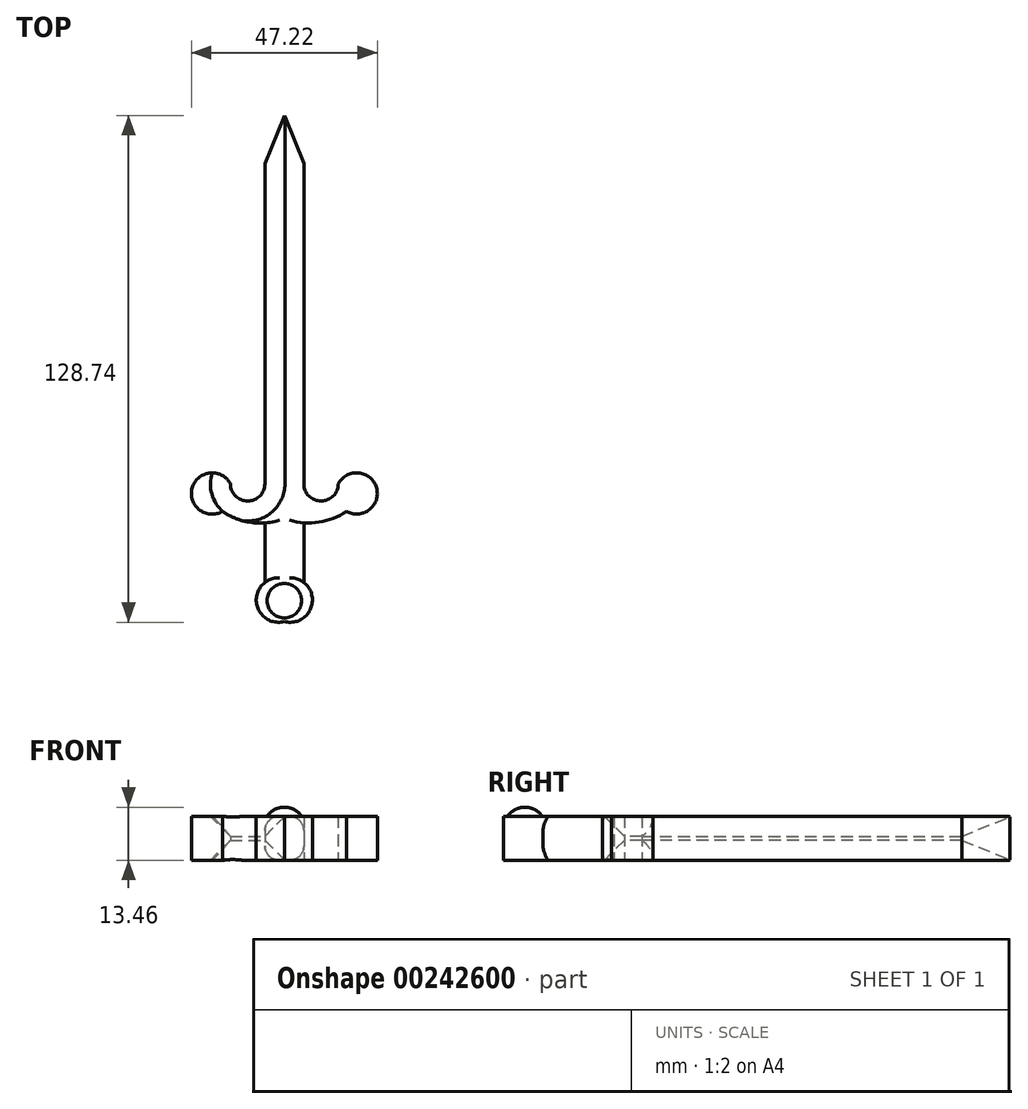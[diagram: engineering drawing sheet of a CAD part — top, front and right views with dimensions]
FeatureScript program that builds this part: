
annotation { "Feature Type Name" : "Feature", "Feature Type Description" : "" }
export const myFeature = defineFeature(function(context is Context, id is Id, definition is map)
    precondition{}
    {
        {
            var Q0;
            Q0=qCreatedBy(makeId("Top.planeOp"),FACE);
            var sketch = newSketch(context, id + "F0", { "sketchPlane" : qUnion([Q0])});
            skLineSegment(sketch, "E0", {"start": v(0, 64.85) * mm, "end": v(4.96, 52.61) * mm});
            skLineSegment(sketch, "E1", {"start": v(4.96, 52.61) * mm, "end": v(4.96, -28.71) * mm});
            skArc(sketch, "E2", {"start": v(4.96, -28.71) * mm, "mid": v(9.33, -33.08) * mm, "end": v(13.7, -28.71) * mm});
            skArc(sketch, "E3", {"start": v(15.74, -35.7) * mm, "mid": v(23.4, -29.68) * mm, "end": v(13.7, -28.71) * mm});
            skArc(sketch, "E4", {"start": v(4.96, -38.62) * mm, "mid": v(10.6, -38.07) * mm, "end": v(15.74, -35.7) * mm});
            skLineSegment(sketch, "E5", {"start": v(4.96, -38.62) * mm, "end": v(4.96, -53.78) * mm});
            skArc(sketch, "E6", {"start": v(0, -63.69) * mm, "mid": v(6.54, -60.76) * mm, "end": v(4.96, -53.78) * mm});
            skLineSegment(sketch, "E7.MirrorCS", {"start": v(0, 64.85) * mm, "end": v(-4.96, 52.61) * mm});
            skLineSegment(sketch, "E8.MirrorCS", {"start": v(-4.96, 52.61) * mm, "end": v(-4.96, -28.71) * mm});
            skArc(sketch, "E9.MirrorCS", {"start": v(-4.96, -28.71) * mm, "mid": v(-9.33, -33.08) * mm, "end": v(-13.7, -28.71) * mm});
            skArc(sketch, "E10.MirrorCS", {"start": v(-15.74, -35.7) * mm, "mid": v(-23.4, -29.68) * mm, "end": v(-13.7, -28.71) * mm});
            skArc(sketch, "E11.MirrorCS", {"start": v(-4.96, -38.62) * mm, "mid": v(-10.6, -38.07) * mm, "end": v(-15.74, -35.7) * mm});
            skLineSegment(sketch, "E12.MirrorCS", {"start": v(-4.96, -38.62) * mm, "end": v(-4.96, -53.78) * mm});
            skArc(sketch, "E13.MirrorCS", {"start": v(0, -63.69) * mm, "mid": v(-6.54, -60.76) * mm, "end": v(-4.96, -53.78) * mm});
            skSolve(sketch);
        }
        {
            var Q0;
            Q0=makeQuery(id+"F0.imprint","IMPRINT",FACE,{"disambiguationData":[TD([[makeQuery(id+"F0.imprint","IMPRINT",EDGE,{"derivedFrom":sQuery(id+"F0.wireOp",EDGE,"E0")}),-1.0]])]});
            extrude(context, id + "F1", {"entities" : qUnion([Q0]), "depth" : 11.18 * mm});
        }
        {
            var Q0;
            Q0=makeQuery(id+"F1.opExtrude","CAP_EDGE",EDGE,{"disambiguationData":[OSD([sQuery(id+"F0.wireOp",EDGE,"E8.MirrorCS")])],"isStart":false});
            var Q1;
            Q1=makeQuery(id+"F1.opExtrude","CAP_EDGE",EDGE,{"disambiguationData":[OSD([sQuery(id+"F0.wireOp",EDGE,"E1")])],"isStart":false});
            var Q2;
            Q2=makeQuery(id+"F1.opExtrude","CAP_EDGE",EDGE,{"disambiguationData":[OSD([sQuery(id+"F0.wireOp",EDGE,"E8.MirrorCS")])],"isStart":true});
            var Q3;
            Q3=makeQuery(id+"F1.opExtrude","CAP_EDGE",EDGE,{"disambiguationData":[OSD([sQuery(id+"F0.wireOp",EDGE,"E1")])],"isStart":true});
            chamfer(context, id + "F2", {"entities" : qUnion([Q0, Q1, Q2, Q3]), "width" : 5.08 * mm, "tangentPropagation" : true});
        }
        {
            var Q0;
            Q0=makeQuery(id+"F1.opExtrude","CAP_EDGE",EDGE,{"disambiguationData":[OSD([sQuery(id+"F0.wireOp",EDGE,"E12.MirrorCS")])],"isStart":false});
            fillet(context, id + "F3", {"entities" : qUnion([Q0]), "radius" : 3.68 * mm, "tangentPropagation" : true, "allowEdgeOverflow" : false});
        }
        {
            var Q0;
            Q0=makeQuery(id+"F1.opExtrude","CAP_EDGE",EDGE,{"disambiguationData":[OSD([sQuery(id+"F0.wireOp",EDGE,"E5")])],"isStart":false});
            var Q1;
            Q1=makeQuery(id+"F1.opExtrude","CAP_EDGE",EDGE,{"disambiguationData":[OSD([sQuery(id+"F0.wireOp",EDGE,"E5")])],"isStart":true});
            var Q2;
            Q2=makeQuery(id+"F1.opExtrude","CAP_EDGE",EDGE,{"disambiguationData":[OSD([sQuery(id+"F0.wireOp",EDGE,"E12.MirrorCS")])],"isStart":true});
            fillet(context, id + "F4", {"entities" : qUnion([Q0, Q1, Q2]), "radius" : 3.68 * mm, "tangentPropagation" : true, "allowEdgeOverflow" : false});
        }
        {
            var Q0;
            Q0=makeQuery(id+"F2.opChamfer","SPLIT",FACE,{"disambiguationData":[OD(2.0)],"derivedFrom":makeQuery(id+"F1.opExtrude","CAP_FACE",FACE,{"disambiguationData":[OSD([sQuery(id+"F0.wireOp",EDGE,"E0"),sQuery(id+"F0.wireOp",EDGE,"E2"),sQuery(id+"F0.wireOp",EDGE,"E3"),sQuery(id+"F0.wireOp",EDGE,"E4"),sQuery(id+"F0.wireOp",EDGE,"E5"),sQuery(id+"F0.wireOp",EDGE,"E6"),sQuery(id+"F0.wireOp",EDGE,"E1"),sQuery(id+"F0.wireOp",EDGE,"E7.MirrorCS"),sQuery(id+"F0.wireOp",EDGE,"E8.MirrorCS"),sQuery(id+"F0.wireOp",EDGE,"E9.MirrorCS"),sQuery(id+"F0.wireOp",EDGE,"E10.MirrorCS"),sQuery(id+"F0.wireOp",EDGE,"E11.MirrorCS"),sQuery(id+"F0.wireOp",EDGE,"E12.MirrorCS"),sQuery(id+"F0.wireOp",EDGE,"E13.MirrorCS")])],"isStart":false})});
            var sketch = newSketch(context, id + "F5", { "sketchPlane" : qUnion([Q0])});
            skCircle(sketch, "E14", {"center": v(0, -58.38) * mm, "radius": 4.38 * mm});
            skSolve(sketch);
        }
        {
            var Q0;
            Q0=makeQuery(id+"F5.imprint","IMPRINT",FACE,{"disambiguationData":[TD([[makeQuery(id+"F5.imprint","IMPRINT",EDGE,{"derivedFrom":sQuery(id+"F5.wireOp",EDGE,"E14")}),1.0]])]});
            extrude(context, id + "F6", {"entities" : qUnion([Q0]), "operationType" : NewBodyOperationType.ADD, "depth" : 2.3 * mm});
        }
        {
            var Q0;
            Q0=makeQuery(id+"F6.opExtrude","CAP_EDGE",EDGE,{"disambiguationData":[OSD([sQuery(id+"F5.wireOp",EDGE,"E14")])],"isStart":false});
            fillet(context, id + "F7", {"entities" : qUnion([Q0]), "radius" : 5.08 * mm, "tangentPropagation" : true, "allowEdgeOverflow" : false});
        }
    });
